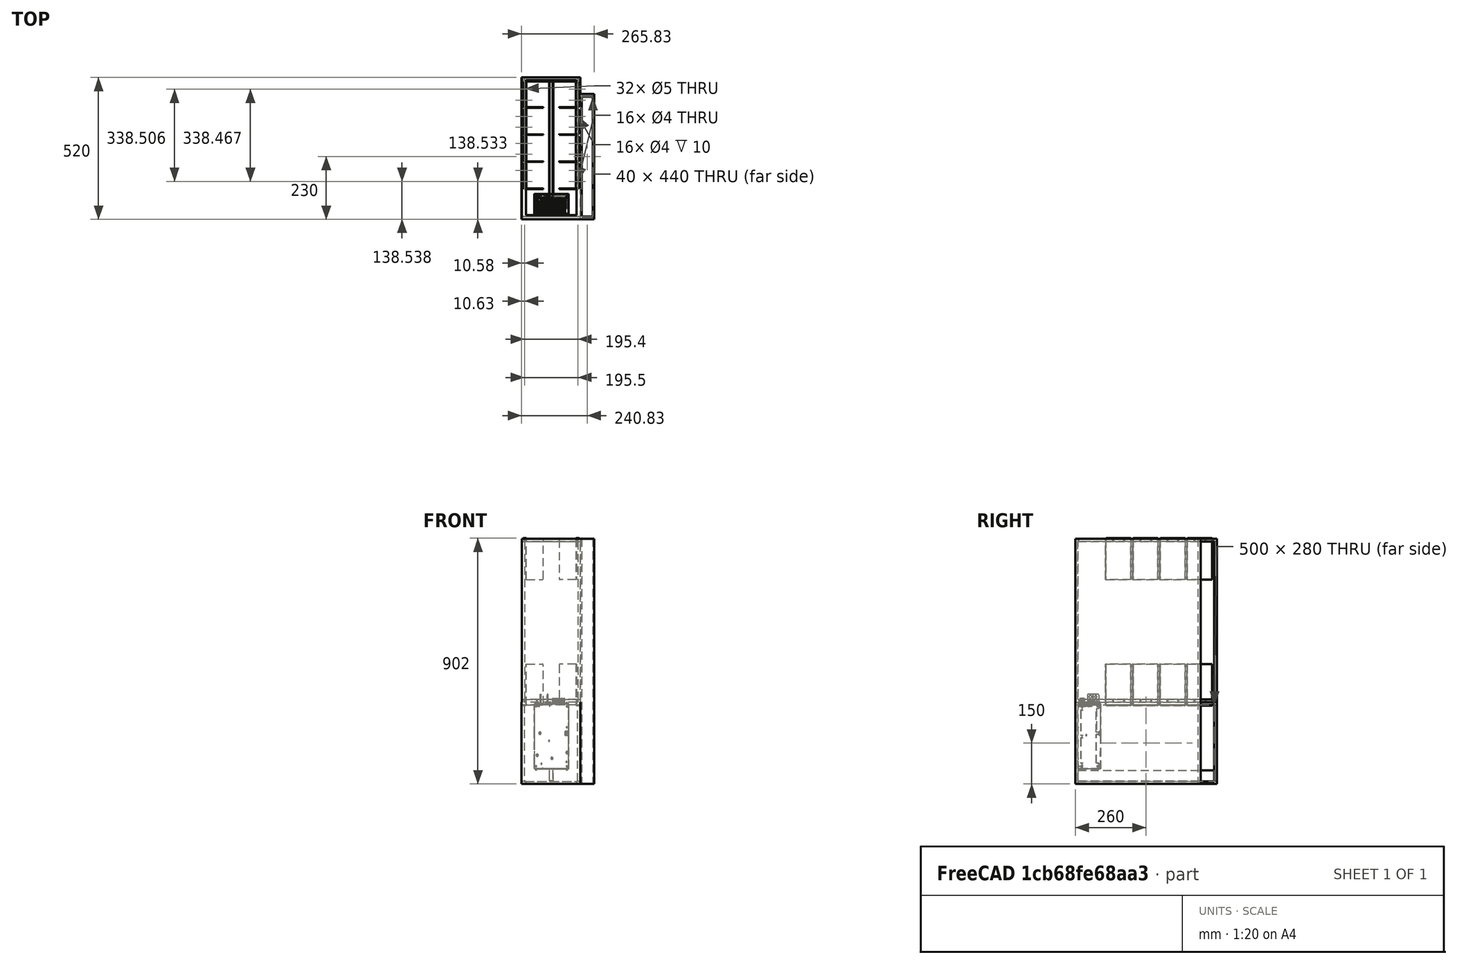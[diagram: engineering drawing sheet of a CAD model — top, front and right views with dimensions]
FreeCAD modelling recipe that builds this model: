
FCSTD DOCUMENT  (FreeCAD 0.16R6698 (Git))
Label: Assembly serveur 1
License: All rights reserved
LicenseURL: http://en.wikipedia.org/wiki/All_rights_reserved
objects: App::FeaturePython×30, Part::FeaturePython×13
note: 13 computed .brp shape members not serialized (recipe doc carries the construction recipe); baked Part::Feature solids carry a one-line shape summary decoded from their .brp

FEATURE [Part::FeaturePython] rack_01  # a2plus imported part (geometry in sourceFile) (typed FeaturePython)
  fixedPosition = true
  sourceFile = <userpath>/Documents/rack.fcstd
  timeLastImport = 1.4628e+09
  updateColors = true
FEATURE [Part::FeaturePython] import_01  label="Glissière droite_01"  # a2plus imported part (geometry in sourceFile) (typed FeaturePython)
  Placement = pos=(92.5,187.4,517.179) rot=(-0.57735,-0.57735,0.57735;2.0944rad)
  fixedPosition = false
  sourceFile = <userpath>/Documents/Glissière droite.fcstd
  timeLastImport = 1.4628e+09
  updateColors = true
FEATURE [App::FeaturePython] planeConstraint01  # a2plus constraint (typed FeaturePython)
  Object1 = import_01
  Object2 = rack_01
  SubElement1 = Face21
  SubElement2 = Face10
  Type = plane
  directionConstraint = 1
  offset = 0
FEATURE [App::FeaturePython] planeConstraint01_mirror  label="planeConstraint01_"  # a2plus constraint (typed FeaturePython)
  Object1 = import_01
  Object2 = rack_01
  SubElement1 = Face21
  SubElement2 = Face10
  Type = plane
  directionConstraint = 1
  offset = 0
FEATURE [App::FeaturePython] planeConstraint02  # a2plus constraint (typed FeaturePython)
  Object1 = import_01
  Object2 = rack_01
  SubElement1 = Face11
  SubElement2 = Face33
  Type = plane
  directionConstraint = 1
  offset = 0
FEATURE [App::FeaturePython] planeConstraint02_mirror  label="planeConstraint02_"  # a2plus constraint (typed FeaturePython)
  Object1 = import_01
  Object2 = rack_01
  SubElement1 = Face11
  SubElement2 = Face33
  Type = plane
  directionConstraint = 1
  offset = 0
FEATURE [Part::FeaturePython] Array  # Draft array (typed FeaturePython)
  Angle = 360
  ArrayType = 0
  Axis = (0,0,1)
  Base = -> import_01
  Center = (0,0,0)
  Fuse = false
  IntervalAxis = (0,0,0)
  IntervalX = (1,0,0)
  IntervalY = (0,-99.4891,0)
  IntervalZ = (0,0,0)
  NumberPolar = 1
  NumberX = 1
  NumberY = 4
  NumberZ = 1
FEATURE [Part::FeaturePython] import_02  label="Glissière gauche_01"  # a2plus imported part (geometry in sourceFile) (typed FeaturePython)
  Placement = pos=(-92.5,206.65,517.179) rot=(-0.57735,0.57735,-0.57735;2.0944rad)
  fixedPosition = false
  sourceFile = <userpath>/Documents/Glissière gauche.fcstd
  timeLastImport = 1.4628e+09
  updateColors = true
FEATURE [App::FeaturePython] planeConstraint03  # a2plus constraint (typed FeaturePython)
  Object1 = import_02
  Object2 = rack_01
  SubElement1 = Face19
  SubElement2 = Face10
  Type = plane
  directionConstraint = 1
  offset = 0
FEATURE [App::FeaturePython] planeConstraint03_mirror  label="planeConstraint03_"  # a2plus constraint (typed FeaturePython)
  Object1 = import_02
  Object2 = rack_01
  SubElement1 = Face19
  SubElement2 = Face10
  Type = plane
  directionConstraint = 1
  offset = 0
FEATURE [App::FeaturePython] planeConstraint04  # a2plus constraint (typed FeaturePython)
  Object1 = import_02
  Object2 = rack_01
  SubElement1 = Face11
  SubElement2 = Face32
  Type = plane
  directionConstraint = 1
  offset = 0
FEATURE [App::FeaturePython] planeConstraint04_mirror  label="planeConstraint04_"  # a2plus constraint (typed FeaturePython)
  Object1 = import_02
  Object2 = rack_01
  SubElement1 = Face11
  SubElement2 = Face32
  Type = plane
  directionConstraint = 1
  offset = 0
FEATURE [Part::FeaturePython] Array001  # Draft array (typed FeaturePython)
  Angle = 360
  ArrayType = 0
  Axis = (0,0,1)
  Base = -> import_02
  Center = (0,0,0)
  Fuse = false
  IntervalAxis = (0,0,0)
  IntervalX = (1,0,0)
  IntervalY = (0,-99.4891,0)
  IntervalZ = (0,0,0)
  NumberPolar = 1
  NumberX = 1
  NumberY = 4
  NumberZ = 1
FEATURE [Part::FeaturePython] import_03  label="Glissière droite_02"  # a2plus imported part (geometry in sourceFile) (typed FeaturePython)
  Placement = pos=(-92.5,187.439,72.8206) rot=(0.57735,0.57735,0.57735;2.0944rad)
  fixedPosition = false
  sourceFile = <userpath>/Documents/Glissière droite.fcstd
  timeLastImport = 1.4628e+09
  updateColors = true
FEATURE [App::FeaturePython] planeConstraint05  # a2plus constraint (typed FeaturePython)
  Object1 = import_03
  Object2 = rack_01
  SubElement1 = Face21
  SubElement2 = Face77
  Type = plane
  directionConstraint = 1
  offset = 0
FEATURE [App::FeaturePython] planeConstraint05_mirror  label="planeConstraint05_"  # a2plus constraint (typed FeaturePython)
  Object1 = import_03
  Object2 = rack_01
  SubElement1 = Face21
  SubElement2 = Face77
  Type = plane
  directionConstraint = 1
  offset = 0
FEATURE [App::FeaturePython] planeConstraint06  # a2plus constraint (typed FeaturePython)
  Object1 = import_03
  Object2 = rack_01
  SubElement1 = Face11
  SubElement2 = Face82
  Type = plane
  directionConstraint = 1
  offset = 0
FEATURE [App::FeaturePython] planeConstraint06_mirror  label="planeConstraint06_"  # a2plus constraint (typed FeaturePython)
  Object1 = import_03
  Object2 = rack_01
  SubElement1 = Face11
  SubElement2 = Face82
  Type = plane
  directionConstraint = 1
  offset = 0
FEATURE [App::FeaturePython] planeConstraint07  # a2plus constraint (typed FeaturePython)
  Object1 = import_03
  Object2 = Array001
  SubElement1 = Face5
  SubElement2 = Face5
  Type = plane
  directionConstraint = 0
  offset = 0
FEATURE [App::FeaturePython] planeConstraint07_mirror  label="planeConstraint07_"  # a2plus constraint (typed FeaturePython)
  Object1 = import_03
  Object2 = Array001
  SubElement1 = Face5
  SubElement2 = Face5
  Type = plane
  directionConstraint = 0
  offset = 0
FEATURE [Part::FeaturePython] Array002  # Draft array (typed FeaturePython)
  Angle = 360
  ArrayType = 0
  Axis = (0,0,1)
  Base = -> import_03
  Center = (0,0,0)
  Fuse = false
  IntervalAxis = (0,0,0)
  IntervalX = (1,0,0)
  IntervalY = (0,-99.4891,0)
  IntervalZ = (0,0,0)
  NumberPolar = 1
  NumberX = 1
  NumberY = 4
  NumberZ = 1
FEATURE [Part::FeaturePython] import_04  label="Glissière gauche_02"  # a2plus imported part (geometry in sourceFile) (typed FeaturePython)
  Placement = pos=(92.5,206.611,72.8206) rot=(0.57735,-0.57735,-0.57735;2.0944rad)
  fixedPosition = false
  sourceFile = <userpath>/Documents/Glissière gauche.fcstd
  timeLastImport = 1.4628e+09
  updateColors = true
FEATURE [App::FeaturePython] planeConstraint08  # a2plus constraint (typed FeaturePython)
  Object1 = import_04
  Object2 = rack_01
  SubElement1 = Face19
  SubElement2 = Face77
  Type = plane
  directionConstraint = 1
  offset = 0
FEATURE [App::FeaturePython] planeConstraint08_mirror  label="planeConstraint08_"  # a2plus constraint (typed FeaturePython)
  Object1 = import_04
  Object2 = rack_01
  SubElement1 = Face19
  SubElement2 = Face77
  Type = plane
  directionConstraint = 1
  offset = 0
FEATURE [App::FeaturePython] planeConstraint09  # a2plus constraint (typed FeaturePython)
  Object1 = import_04
  Object2 = rack_01
  SubElement1 = Face11
  SubElement2 = Face86
  Type = plane
  directionConstraint = 1
  offset = 0
FEATURE [App::FeaturePython] planeConstraint09_mirror  label="planeConstraint09_"  # a2plus constraint (typed FeaturePython)
  Object1 = import_04
  Object2 = rack_01
  SubElement1 = Face11
  SubElement2 = Face86
  Type = plane
  directionConstraint = 1
  offset = 0
FEATURE [App::FeaturePython] planeConstraint10  # a2plus constraint (typed FeaturePython)
  Object1 = import_04
  Object2 = Array
  SubElement1 = Face5
  SubElement2 = Face5
  Type = plane
  directionConstraint = 0
  offset = 0
FEATURE [App::FeaturePython] planeConstraint10_mirror  label="planeConstraint10_"  # a2plus constraint (typed FeaturePython)
  Object1 = import_04
  Object2 = Array
  SubElement1 = Face5
  SubElement2 = Face5
  Type = plane
  directionConstraint = 0
  offset = 0
FEATURE [Part::FeaturePython] Array003  # Draft array (typed FeaturePython)
  Angle = 360
  ArrayType = 0
  Axis = (0,0,1)
  Base = -> import_04
  Center = (0,0,0)
  Fuse = false
  IntervalAxis = (0,0,0)
  IntervalX = (1,0,0)
  IntervalY = (0,-99.4891,0)
  IntervalZ = (0,0,0)
  NumberPolar = 1
  NumberX = 1
  NumberY = 4
  NumberZ = 1
FEATURE [Part::FeaturePython] u_01  # a2plus imported part (geometry in sourceFile) (typed FeaturePython)
  Placement = pos=(0,-250,-265) rot=(0,0.707107,0.707107;3.14159rad)
  fixedPosition = false
  sourceFile = <userpath>/Documents/u.fcstd
  timeLastImport = 1.4628e+09
  updateColors = true
FEATURE [App::FeaturePython] planeConstraint11  # a2plus constraint (typed FeaturePython)
  Object1 = u_01
  Object2 = rack_01
  SubElement1 = Face9
  SubElement2 = Face112
  Type = plane
  directionConstraint = 1
  offset = 0
FEATURE [App::FeaturePython] planeConstraint11_mirror  label="planeConstraint11_"  # a2plus constraint (typed FeaturePython)
  Object1 = u_01
  Object2 = rack_01
  SubElement1 = Face9
  SubElement2 = Face112
  Type = plane
  directionConstraint = 1
  offset = 0
FEATURE [App::FeaturePython] planeConstraint12  # a2plus constraint (typed FeaturePython)
  Object1 = u_01
  Object2 = rack_01
  SubElement1 = Face7
  SubElement2 = Face79
  Type = plane
  directionConstraint = 1
  offset = 0
FEATURE [App::FeaturePython] planeConstraint12_mirror  label="planeConstraint12_"  # a2plus constraint (typed FeaturePython)
  Object1 = u_01
  Object2 = rack_01
  SubElement1 = Face7
  SubElement2 = Face79
  Type = plane
  directionConstraint = 1
  offset = 0
FEATURE [Part::FeaturePython] hws1000_outline_01  # a2plus imported part (geometry in sourceFile) (typed FeaturePython)
  Placement = pos=(1,-250,-125) rot=(0,0,1;0rad)
  fixedPosition = false
  sourceFile = <userpath>/Documents/hws1000_outline.fcstd
  timeLastImport = 1.4628e+09
  updateColors = true
FEATURE [App::FeaturePython] planeConstraint13  # a2plus constraint (typed FeaturePython)
  Object1 = hws1000_outline_01
  Object2 = rack_01
  SubElement1 = Face4956
  SubElement2 = Face112
  Type = plane
  directionConstraint = 1
  offset = 0
FEATURE [App::FeaturePython] planeConstraint13_mirror  label="planeConstraint13_"  # a2plus constraint (typed FeaturePython)
  Object1 = hws1000_outline_01
  Object2 = rack_01
  SubElement1 = Face4956
  SubElement2 = Face112
  Type = plane
  directionConstraint = 1
  offset = 0
FEATURE [Part::FeaturePython] ServeurFB_01  # a2plus imported part (geometry in sourceFile) (typed FeaturePython)
  Placement = pos=(0,152.005,-163.827) rot=(0,-0.707107,-0.707107;3.14159rad)
  fixedPosition = false
  sourceFile = <userpath>/Documents/ServeurFB.fcstd
  timeLastImport = 1.4628e+09
  updateColors = true
FEATURE [App::FeaturePython] planeConstraint14  # a2plus constraint (typed FeaturePython)
  Object1 = ServeurFB_01
  Object2 = Array003
  SubElement1 = Face498
  SubElement2 = Face5
  Type = plane
  directionConstraint = 1
  offset = 0
FEATURE [App::FeaturePython] planeConstraint14_mirror  label="planeConstraint14_"  # a2plus constraint (typed FeaturePython)
  Object1 = ServeurFB_01
  Object2 = Array003
  SubElement1 = Face498
  SubElement2 = Face5
  Type = plane
  directionConstraint = 1
  offset = 0
FEATURE [App::FeaturePython] planeConstraint15  # a2plus constraint (typed FeaturePython)
  Object1 = ServeurFB_01
  Object2 = Array
  SubElement1 = Face374
  SubElement2 = Face22
  Type = plane
  directionConstraint = 0
  offset = 0
FEATURE [App::FeaturePython] planeConstraint15_mirror  label="planeConstraint15_"  # a2plus constraint (typed FeaturePython)
  Object1 = ServeurFB_01
  Object2 = Array
  SubElement1 = Face374
  SubElement2 = Face22
  Type = plane
  directionConstraint = 0
  offset = 0
FEATURE [Part::FeaturePython] Array004  # Draft array (typed FeaturePython)
  Angle = 360
  ArrayType = 0
  Axis = (0,0,1)
  Base = -> ServeurFB_01
  Center = (0,0,0)
  Fuse = false
  IntervalAxis = (0,0,0)
  IntervalX = (1,0,0)
  IntervalY = (0,-99.4891,0)
  IntervalZ = (0,0,0)
  NumberPolar = 1
  NumberX = 1
  NumberY = 4
  NumberZ = 1
